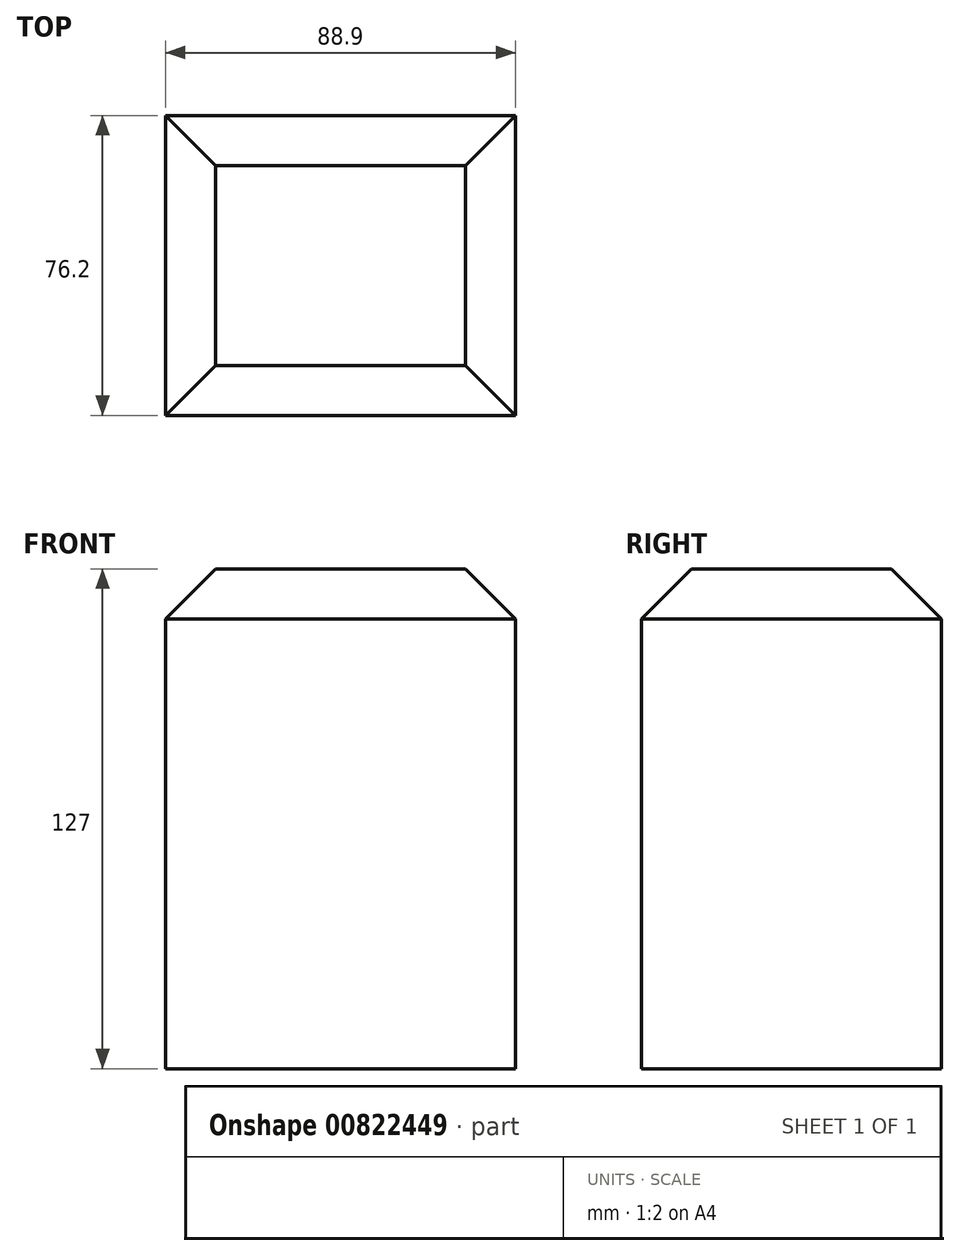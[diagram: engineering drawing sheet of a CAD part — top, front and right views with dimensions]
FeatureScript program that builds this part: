
annotation { "Feature Type Name" : "Feature", "Feature Type Description" : "" }
export const myFeature = defineFeature(function(context is Context, id is Id, definition is map)
    precondition{}
    {
        {
            var Q0;
            Q0=qCreatedBy(makeId("Top.planeOp"),FACE);
            var sketch = newSketch(context, id + "F0", { "sketchPlane" : qUnion([Q0])});
            skLineSegment(sketch, "E0.bottom", {"start": v(0, 0) * mm, "end": v(88.9, 0) * mm});
            skLineSegment(sketch, "E0.top", {"start": v(0, 76.2) * mm, "end": v(88.9, 76.2) * mm});
            skLineSegment(sketch, "E0.left", {"start": v(0, 0) * mm, "end": v(0, 76.2) * mm});
            skLineSegment(sketch, "E0.right", {"start": v(88.9, 0) * mm, "end": v(88.9, 76.2) * mm});
            skSolve(sketch);
        }
        {
            var Q0;
            Q0=makeQuery(id+"F0.imprint","IMPRINT",FACE,{"disambiguationData":[TD([[makeQuery(id+"F0.imprint","IMPRINT",EDGE,{"derivedFrom":sQuery(id+"F0.wireOp",EDGE,"E0.bottom")}),1.0]])]});
            extrude(context, id + "F1", {"entities" : qUnion([Q0]), "depth" : 127 * mm, "offsetDistance" : 25.4 * mm});
        }
        {
            var Q0;
            Q0=makeQuery(id+"F1.opExtrude","CAP_EDGE",EDGE,{"disambiguationData":[OSD([sQuery(id+"F0.wireOp",EDGE,"E0.bottom")])],"isStart":false});
            var Q1;
            Q1=makeQuery(id+"F1.opExtrude","CAP_EDGE",EDGE,{"disambiguationData":[OSD([sQuery(id+"F0.wireOp",EDGE,"E0.right")])],"isStart":false});
            var Q2;
            Q2=makeQuery(id+"F1.opExtrude","CAP_EDGE",EDGE,{"disambiguationData":[OSD([sQuery(id+"F0.wireOp",EDGE,"E0.top")])],"isStart":false});
            var Q3;
            Q3=makeQuery(id+"F1.opExtrude","CAP_EDGE",EDGE,{"disambiguationData":[OSD([sQuery(id+"F0.wireOp",EDGE,"E0.left")])],"isStart":false});
            chamfer(context, id + "F2", {"entities" : qUnion([Q0, Q1, Q2, Q3]), "chamferType" : ChamferType.OFFSET_ANGLE, "width" : 12.7 * mm, "oppositeDirection" : false, "angle" : 45 * degree, "tangentPropagation" : true});
        }
    });
